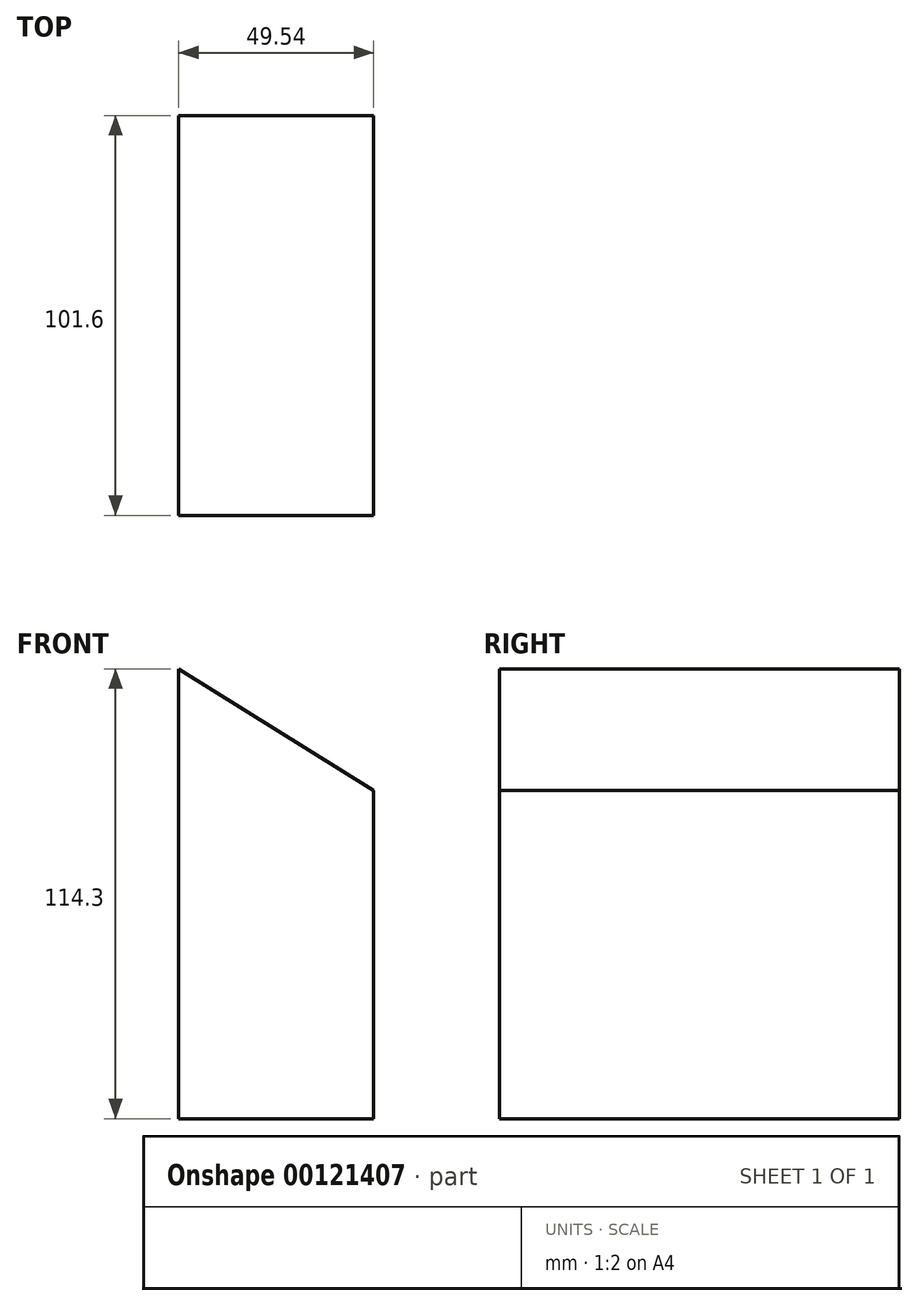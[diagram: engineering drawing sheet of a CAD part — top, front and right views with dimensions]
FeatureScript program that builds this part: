
annotation { "Feature Type Name" : "Feature", "Feature Type Description" : "" }
export const myFeature = defineFeature(function(context is Context, id is Id, definition is map)
    precondition{}
    {
        {
            var Q0;
            Q0=qCreatedBy(makeId("Front.planeOp"),FACE);
            var sketch = newSketch(context, id + "F0", { "sketchPlane" : qUnion([Q0])});
            skLineSegment(sketch, "E0", {"start": v(-24.47, -23.53) * mm, "end": v(-24.47, 90.77) * mm});
            skLineSegment(sketch, "E1.MirrorCS", {"start": v(-24.47, 90.77) * mm, "end": v(25.07, 59.8) * mm});
            skLineSegment(sketch, "E2", {"start": v(25.07, -23.53) * mm, "end": v(-24.47, -23.53) * mm});
            skLineSegment(sketch, "E3", {"start": v(25.07, 59.8) * mm, "end": v(25.07, -23.53) * mm});
            skPoint(sketch, "E4.orphan", {"position": v(31.52, -23.53) * mm});
            skSolve(sketch);
        }
        {
            var Q0;
            Q0=makeQuery(id+"F0.imprint","IMPRINT",FACE,{"disambiguationData":[TD([[makeQuery(id+"F0.imprint","IMPRINT",EDGE,{"derivedFrom":sQuery(id+"F0.wireOp",EDGE,"E0")}),-1.0]])]});
            extrude(context, id + "F1", {"entities" : qUnion([Q0]), "depth" : 101.6 * mm});
        }
    });
